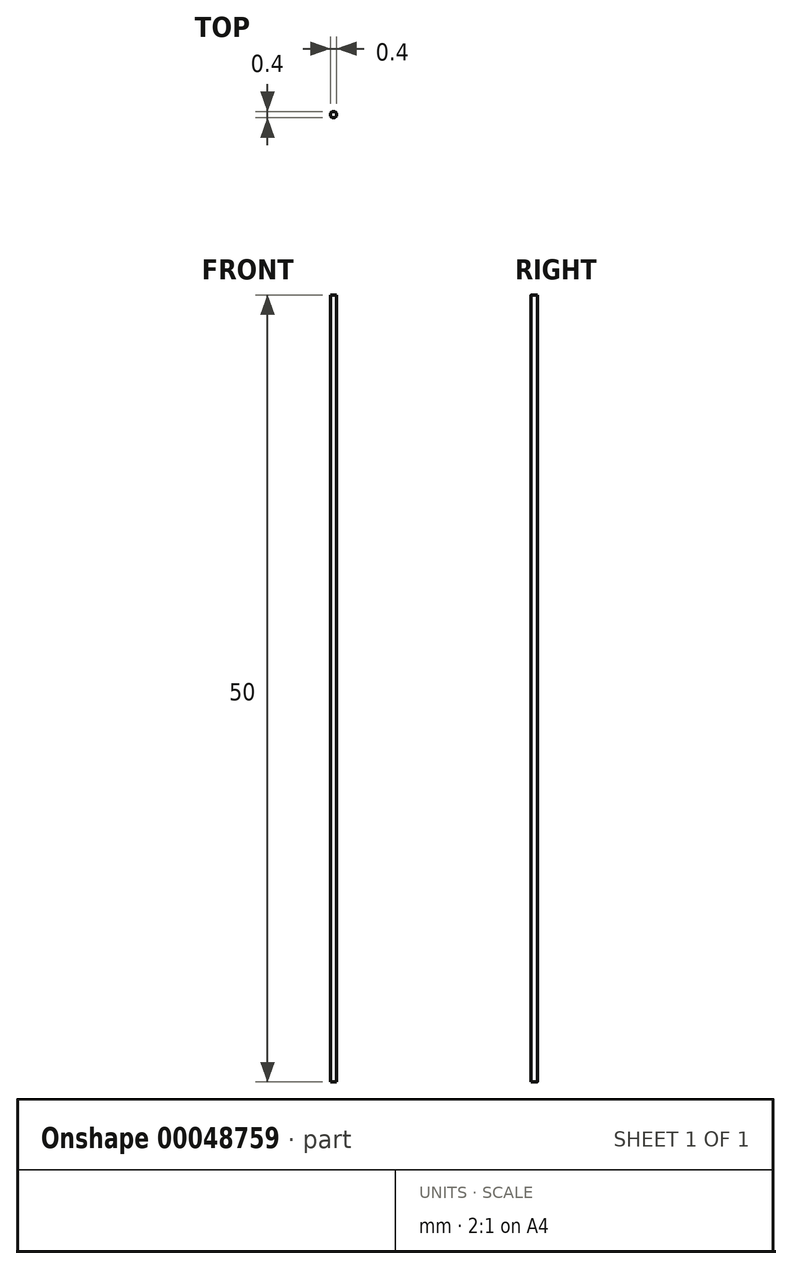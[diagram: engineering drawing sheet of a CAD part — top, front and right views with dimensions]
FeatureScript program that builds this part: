
annotation { "Feature Type Name" : "Feature", "Feature Type Description" : "" }
export const myFeature = defineFeature(function(context is Context, id is Id, definition is map)
    precondition{}
    {
        {
            var Q0;
            Q0=qCreatedBy(makeId("Top.planeOp"),FACE);
            var sketch = newSketch(context, id + "F0", { "sketchPlane" : qUnion([Q0])});
            skCircle(sketch, "E0", {"center": v(0, 0) * mm, "radius": 0.2 * mm});
            skSolve(sketch);
        }
        {
            var Q0;
            Q0 = qSketchRegion(id + "F0", true);
            extrude(context, id + "F1", {"entities" : qUnion([Q0]), "depth" : 50 * mm});
        }
    });
